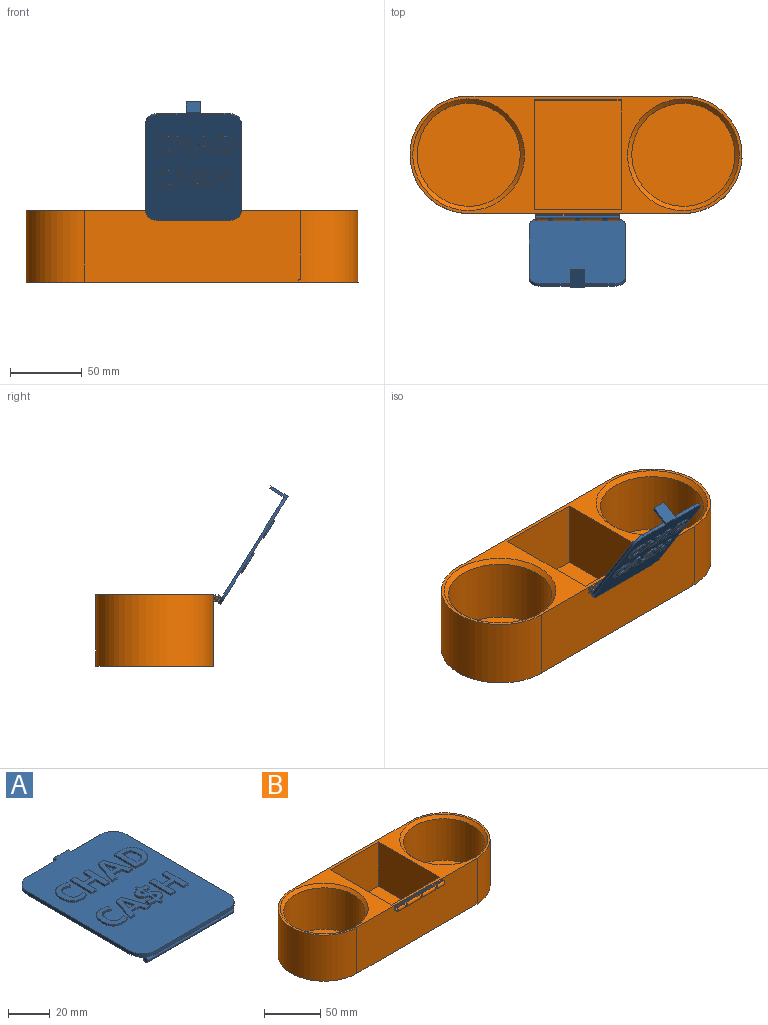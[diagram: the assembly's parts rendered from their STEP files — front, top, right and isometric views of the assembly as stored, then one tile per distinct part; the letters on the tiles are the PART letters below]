
ASSEMBLY  parts=2 mates=1
PART A: 167 faces, bbox 67.2x89x15 mm
  f0: plane 88.97x67.19mm, normal (0,0,1), area 4974.1mm2, adj f1,f6,f7,f8,f9,f22,f23,f24
  f1: plane 20.08x2mm, normal (0,1,0), area 40.2mm2, adj f0,f5,f23,f28
  f2: cylinder r=1.4mm len=58.64mm, axis (-1,0,0), area 502.5mm2, adj f3,f4,f10,f11,f12,f13,f14,f15
  f3: plane 2.8x2.8mm, normal (1,0,0), area 6.2mm2, adj f2
  f4: plane 2.8x2.8mm, normal (-1,0,0), area 6.2mm2, adj f2
  f5: plane 86.97x67.19mm, normal (0,0,-1), area 5768mm2, adj f1,f6,f7,f8,f9,f10,f11,f12
  f6: plane 50.01x2mm, normal (0,-1,0), area 100mm2, adj f0,f5,f22,f24
  f7: plane 20.08x2mm, normal (0,1,0), area 40.2mm2, adj f0,f5,f25,f29
  f8: plane 69.79x2mm, normal (1,0,0), area 139.6mm2, adj f0,f5,f24,f25
  f9: plane 69.79x2mm, normal (-1,0,0), area 139.6mm2, adj f0,f5,f22,f23
  f10: plane 2x1.6mm, normal (1,0,0), area 2.6mm2, adj f2,f5,f11,f13
  f11: plane 2x1.6mm, normal (0,-1,0), area 3.2mm2, adj f2,f5,f10,f12
  f12: plane 2x1.6mm, normal (-1,0,0), area 2.6mm2, adj f2,f5,f11,f13
  f13: plane 2x1.59mm, normal (0,1,0), area 3.2mm2, adj f2,f5,f10,f12
  f14: plane 2x1.59mm, normal (0,1,0), area 3.2mm2, adj f2,f5,f15,f17
  f15: plane 2x1.6mm, normal (1,0,0), area 2.6mm2, adj f2,f5,f14,f16
  f16: plane 2x1.6mm, normal (0,-1,0), area 3.2mm2, adj f2,f5,f15,f17
  f17: plane 2x1.6mm, normal (-1,0,0), area 2.6mm2, adj f2,f5,f14,f16
  f18: plane 2x1.59mm, normal (0,1,0), area 3.2mm2, adj f2,f5,f19,f21
  f19: plane 2x1.6mm, normal (1,0,0), area 2.6mm2, adj f2,f5,f18,f20
  f20: plane 2x1.6mm, normal (0,-1,0), area 3.2mm2, adj f2,f5,f19,f21
  f21: plane 2x1.6mm, normal (-1,0,0), area 2.6mm2, adj f2,f5,f18,f20
  f22: cylinder r=8.59mm len=8.59mm, axis (0,0,1), area 27mm2, adj f0,f5,f6,f9
  f23: cylinder r=8.59mm len=8.59mm, axis (0,0,-1), area 27mm2, adj f0,f1,f5,f9
  f24: cylinder r=8.59mm len=8.59mm, axis (0,0,-1), area 27mm2, adj f0,f5,f6,f8
  f25: cylinder r=8.59mm len=8.59mm, axis (0,0,1), area 27mm2, adj f0,f5,f7,f8
  f26: plane 12.02x9.85mm, normal (0,-1,0), area 118.4mm2, adj f5,f27,f28,f29
  f27: plane 9.85x2mm, normal (0,0,-1), area 19.7mm2, adj f26,f28,f29,f30
  f28: plane 14.02x2mm, normal (-1,0,0), area 28mm2, adj f0,f1,f26,f27,f30
  f29: plane 14.02x2mm, normal (1,0,0), area 28mm2, adj f0,f7,f26,f27,f30
  f30: plane 14.02x9.85mm, normal (0,1,0), area 138.1mm2, adj f0,f27,f28,f29
  f31: extruded ~2.7x1.31mm, area 3.1mm2, adj f0,f32,f45,f46
  f32: extruded ~1.62x1mm, area 1.7mm2, adj f0,f31,f33,f46
  f33: extruded ~1.65x1mm, area 1.8mm2, adj f0,f32,f34,f46
  f34: plane 2.51x1mm, normal (0.93,-0.37,0), area 2.7mm2, adj f0,f33,f35,f46
  f35: extruded ~4.27x1.02mm, area 4.4mm2, adj f0,f34,f36,f46
  f36: extruded ~3.63x1mm, area 3.8mm2, adj f0,f35,f37,f46
  f37: extruded ~2.62x2.38mm, area 3.6mm2, adj f0,f36,f38,f46
  f38: extruded ~3.99x1mm, area 4.1mm2, adj f0,f37,f39,f46
  f39: extruded ~5.54x1.68mm, area 5.9mm2, adj f0,f38,f40,f46
  f40: extruded ~4.87x1.93mm, area 5.4mm2, adj f0,f39,f41,f46
  f41: extruded ~4.01x1mm, area 4.1mm2, adj f0,f40,f42,f46
  f42: plane 2.59x1mm, normal (1,0,0), area 2.6mm2, adj f0,f41,f43,f46
  f43: extruded ~3.72x1mm, area 3.8mm2, adj f0,f42,f44,f46
  f44: extruded ~4.88x3.66mm, area 7mm2, adj f0,f43,f45,f46
  f45: extruded ~3.65x1mm, area 3.8mm2, adj f0,f31,f44,f46
  f46: plane 14.99x11.11mm, normal (0,0,1), area 74.6mm2, adj f31,f32,f33,f34,f35,f36,f37,f38
  f47: plane 3.08x1mm, normal (0,-1,0), area 3.1mm2, adj f0,f48,f58,f59
  f48: plane 14.58x1mm, normal (1,0,0), area 14.6mm2, adj f0,f47,f49,f59
  f49: plane 3.08x1mm, normal (0,1,0), area 3.1mm2, adj f0,f48,f50,f59
  f50: plane 5.71x1mm, normal (-1,0,0), area 5.7mm2, adj f0,f49,f51,f59
  f51: plane 5.77x1mm, normal (0,1,0), area 5.8mm2, adj f0,f50,f52,f59
  f52: plane 5.71x1mm, normal (1,0,0), area 5.7mm2, adj f0,f51,f53,f59
  f53: plane 3.09x1mm, normal (0,1,0), area 3.1mm2, adj f0,f52,f54,f59
  f54: plane 14.58x1mm, normal (-1,0,0), area 14.6mm2, adj f0,f53,f55,f59
  f55: plane 3.09x1mm, normal (0,-1,0), area 3.1mm2, adj f0,f54,f56,f59
  f56: plane 6.29x1mm, normal (1,0,0), area 6.3mm2, adj f0,f55,f57,f59
  f57: plane 5.77x1mm, normal (0,-1,0), area 5.8mm2, adj f0,f56,f58,f59
  f58: plane 6.29x1mm, normal (-1,0,0), area 6.3mm2, adj f0,f47,f57,f59
  f59: plane 14.58x11.95mm, normal (0,0,1), area 104.8mm2, adj f47,f48,f49,f50,f51,f52,f53,f54
  f60: extruded ~5.33x1.65mm, area 5.6mm2, adj f61,f71,f72,f73
  f61: plane 3.8x1mm, normal (0,1,0), area 3.8mm2, adj f60,f62,f72,f73
  f62: extruded ~6.31x1.88mm, area 6.6mm2, adj f61,f71,f72,f73
  f63: plane 3.47x1.06mm, normal (-0.96,-0.29,0), area 3.6mm2, adj f0,f64,f70,f72
  f64: plane 3.33x1mm, normal (0,-1,0), area 3.3mm2, adj f0,f63,f65,f72
  f65: plane 14.64x5.17mm, normal (0.94,0.33,0), area 15.5mm2, adj f0,f64,f66,f72
  f66: plane 3.78x1mm, normal (0,1,0), area 3.8mm2, adj f0,f65,f67,f72
  f67: plane 14.64x5.15mm, normal (-0.94,0.33,0), area 15.5mm2, adj f0,f66,f68,f72
  f68: plane 3.33x1mm, normal (0,-1,0), area 3.3mm2, adj f0,f67,f69,f72
  f69: plane 3.47x1.06mm, normal (0.96,-0.29,0), area 3.6mm2, adj f0,f68,f70,f72
  f70: plane 5.32x1mm, normal (0,-1,0), area 5.3mm2, adj f0,f63,f69,f72
  f71: extruded ~1x0.98mm, area 1mm2, adj f60,f62,f72,f73
  f72: plane 14.64x14.09mm, normal (0,0,1), area 96.9mm2, adj f60,f61,f62,f63,f64,f65,f66,f67
  f73: plane 6.31x3.8mm, normal (0,0,1), area 11.8mm2, adj f60,f61,f62,f71
  f74: extruded ~4.7x4.15mm, area 7.2mm2, adj f75,f85,f86,f87
  f75: extruded ~4.8x4.47mm, area 7.5mm2, adj f74,f76,f86,f87
  f76: plane 1.32x1mm, normal (0,1,0), area 1.3mm2, adj f75,f77,f86,f87
  f77: plane 9.49x1mm, normal (1,0,0), area 9.5mm2, adj f76,f85,f86,f87
  f78: extruded ~5.51x2.05mm, area 6.1mm2, adj f0,f79,f84,f86
  f79: extruded ~5.27x1.98mm, area 5.8mm2, adj f0,f78,f80,f86
  f80: extruded ~5.55x1.88mm, area 6mm2, adj f0,f79,f81,f86
  f81: plane 4.58x1mm, normal (0,1,0), area 4.6mm2, adj f0,f80,f82,f86
  f82: plane 14.58x1mm, normal (-1,0,0), area 14.6mm2, adj f0,f81,f83,f86
  f83: plane 4.13x1mm, normal (0,-1,0), area 4.1mm2, adj f0,f82,f84,f86
  f84: extruded ~5.92x1.91mm, area 6.4mm2, adj f0,f78,f83,f86
  f85: plane 1.64x1mm, normal (0,-1,0), area 1.6mm2, adj f74,f77,f86,f87
  f86: plane 14.58x12.1mm, normal (0,0,1), area 108.2mm2, adj f74,f75,f76,f77,f78,f79,f80,f81
  f87: plane 9.49x5.79mm, normal (0,0,1), area 48.1mm2, adj f74,f75,f76,f77,f85
  f88: extruded ~2.7x1.31mm, area 3.1mm2, adj f0,f89,f102,f103
  f89: extruded ~1.62x1mm, area 1.7mm2, adj f0,f88,f90,f103
  f90: extruded ~1.65x1mm, area 1.8mm2, adj f0,f89,f91,f103
  f91: plane 2.51x1mm, normal (0.93,-0.37,0), area 2.7mm2, adj f0,f90,f92,f103
  f92: extruded ~4.27x1.02mm, area 4.4mm2, adj f0,f91,f93,f103
  f93: extruded ~3.63x1mm, area 3.8mm2, adj f0,f92,f94,f103
  f94: extruded ~2.62x2.38mm, area 3.6mm2, adj f0,f93,f95,f103
  f95: extruded ~3.99x1mm, area 4.1mm2, adj f0,f94,f96,f103
  f96: extruded ~5.54x1.68mm, area 5.9mm2, adj f0,f95,f97,f103
  f97: extruded ~4.87x1.93mm, area 5.4mm2, adj f0,f96,f98,f103
  f98: extruded ~4.01x1mm, area 4.1mm2, adj f0,f97,f99,f103
  f99: plane 2.59x1mm, normal (1,0,0), area 2.6mm2, adj f0,f98,f100,f103
  f100: extruded ~3.72x1mm, area 3.8mm2, adj f0,f99,f101,f103
  f101: extruded ~4.88x3.66mm, area 7mm2, adj f0,f100,f102,f103
  f102: extruded ~3.65x1mm, area 3.8mm2, adj f0,f88,f101,f103
  f103: plane 14.99x11.11mm, normal (0,0,1), area 74.6mm2, adj f88,f89,f90,f91,f92,f93,f94,f95
  f104: extruded ~5.33x1.65mm, area 5.6mm2, adj f105,f115,f116,f117
  f105: plane 3.8x1mm, normal (0,1,0), area 3.8mm2, adj f104,f106,f116,f117
  f106: extruded ~6.31x1.88mm, area 6.6mm2, adj f105,f115,f116,f117
  f107: plane 3.47x1.06mm, normal (-0.96,-0.29,0), area 3.6mm2, adj f0,f108,f114,f116
  f108: plane 3.33x1mm, normal (0,-1,0), area 3.3mm2, adj f0,f107,f109,f116
  f109: plane 14.64x5.17mm, normal (0.94,0.33,0), area 15.5mm2, adj f0,f108,f110,f116
  f110: plane 3.78x1mm, normal (0,1,0), area 3.8mm2, adj f0,f109,f111,f116
  f111: plane 14.64x5.15mm, normal (-0.94,0.33,0), area 15.5mm2, adj f0,f110,f112,f116
  f112: plane 3.33x1mm, normal (0,-1,0), area 3.3mm2, adj f0,f111,f113,f116
  f113: plane 3.47x1.06mm, normal (0.96,-0.29,0), area 3.6mm2, adj f0,f112,f114,f116
  f114: plane 5.32x1mm, normal (0,-1,0), area 5.3mm2, adj f0,f107,f113,f116
  f115: extruded ~1x0.98mm, area 1mm2, adj f104,f106,f116,f117
  f116: plane 14.64x14.09mm, normal (0,0,1), area 96.9mm2, adj f104,f105,f106,f107,f108,f109,f110,f111
  f117: plane 6.31x3.8mm, normal (0,0,1), area 11.8mm2, adj f104,f105,f106,f115
  f118: extruded ~1x0.72mm, area 0.8mm2, adj f119,f150,f151,f152
  f119: extruded ~1.29x1.04mm, area 1.8mm2, adj f118,f120,f151,f152
  f120: plane 2.34x1mm, normal (-1,0,0), area 2.3mm2, adj f119,f150,f151,f152
  f121: extruded ~1x0.71mm, area 0.8mm2, adj f122,f148,f151,f153
  f122: extruded ~1.36x1.17mm, area 2mm2, adj f121,f123,f151,f153
  f123: plane 2.48x1mm, normal (1,0,0), area 2.5mm2, adj f122,f148,f151,f153
  f124: extruded ~2.55x1.15mm, area 2.9mm2, adj f0,f125,f149,f151
  f125: extruded ~1.54x1mm, area 1.6mm2, adj f0,f124,f126,f151
  f126: extruded ~1.21x1.21mm, area 1.7mm2, adj f0,f125,f127,f151
  f127: extruded ~2.77x1.3mm, area 3.1mm2, adj f0,f126,f128,f151
  f128: plane 2.94x1mm, normal (1,0,0), area 2.9mm2, adj f0,f127,f129,f151
  f129: extruded ~3.19x1mm, area 3.3mm2, adj f0,f128,f130,f151
  f130: plane 2.33x1mm, normal (0.93,-0.37,0), area 2.5mm2, adj f0,f129,f131,f151
  f131: extruded ~4.13x1mm, area 4.3mm2, adj f0,f130,f132,f151
  f132: plane 1.48x1mm, normal (1,0,0), area 1.5mm2, adj f0,f131,f133,f151
  f133: plane 1.37x1mm, normal (0,1,0), area 1.4mm2, adj f0,f132,f134,f151
  f134: plane 1.53x1mm, normal (-1,0,0), area 1.5mm2, adj f0,f133,f135,f151
  f135: extruded ~3.16x1.13mm, area 3.4mm2, adj f0,f134,f136,f151
  f136: extruded ~2.38x1.13mm, area 2.7mm2, adj f0,f135,f137,f151
  f137: extruded ~2.26x1mm, area 2.5mm2, adj f0,f136,f138,f151
  f138: extruded ~2.8x1.69mm, area 3.3mm2, adj f0,f137,f139,f151
  f139: plane 1x0.67mm, normal (-0.36,-0.93,0), area 0.7mm2, adj f0,f138,f140,f151
  f140: plane 3.09x1mm, normal (-1,0,0), area 3.1mm2, adj f0,f139,f141,f151
  f141: extruded ~2.18x1mm, area 2.2mm2, adj f0,f140,f142,f151
  f142: extruded ~2.09x1mm, area 2.2mm2, adj f0,f141,f143,f151
  f143: plane 2.63x1mm, normal (-1,0,0), area 2.6mm2, adj f0,f142,f144,f151
  f144: extruded ~4.27x1mm, area 4.4mm2, adj f0,f143,f145,f151
  f145: plane 2x1mm, normal (-1,0,0), area 2mm2, adj f0,f144,f146,f151
  f146: plane 1.37x1mm, normal (0,-1,0), area 1.4mm2, adj f0,f145,f147,f151
  f147: plane 2.05x1mm, normal (1,0,0), area 2mm2, adj f0,f146,f149,f151
  f148: extruded ~1.02x1mm, area 1.2mm2, adj f121,f123,f151,f153
  f149: extruded ~3.21x1.15mm, area 3.5mm2, adj f0,f124,f147,f151
  f150: extruded ~1x0.98mm, area 1.1mm2, adj f118,f120,f151,f152
  f151: plane 16.68x10.01mm, normal (0,0,1), area 88.4mm2, adj f118,f119,f120,f121,f122,f123,f124,f125
  f152: plane 2.34x1.29mm, normal (0,0,1), area 2.2mm2, adj f118,f119,f120,f150
  f153: plane 2.48x1.36mm, normal (0,0,1), area 2.4mm2, adj f121,f122,f123,f148
  f154: plane 3.08x1mm, normal (0,-1,0), area 3.1mm2, adj f0,f155,f165,f166
  f155: plane 14.58x1mm, normal (1,0,0), area 14.6mm2, adj f0,f154,f156,f166
  f156: plane 3.08x1mm, normal (0,1,0), area 3.1mm2, adj f0,f155,f157,f166
  f157: plane 5.71x1mm, normal (-1,0,0), area 5.7mm2, adj f0,f156,f158,f166
  f158: plane 5.77x1mm, normal (0,1,0), area 5.8mm2, adj f0,f157,f159,f166
  f159: plane 5.71x1mm, normal (1,0,0), area 5.7mm2, adj f0,f158,f160,f166
  f160: plane 3.09x1mm, normal (0,1,0), area 3.1mm2, adj f0,f159,f161,f166
  f161: plane 14.58x1mm, normal (-1,0,0), area 14.6mm2, adj f0,f160,f162,f166
  f162: plane 3.09x1mm, normal (0,-1,0), area 3.1mm2, adj f0,f161,f163,f166
  f163: plane 6.29x1mm, normal (1,0,0), area 6.3mm2, adj f0,f162,f164,f166
  f164: plane 5.77x1mm, normal (0,-1,0), area 5.8mm2, adj f0,f163,f165,f166
  f165: plane 6.29x1mm, normal (-1,0,0), area 6.3mm2, adj f0,f154,f164,f166
  f166: plane 14.58x11.95mm, normal (0,0,1), area 104.8mm2, adj f154,f155,f156,f157,f158,f159,f160,f161
PART B: 41 faces, bbox 232x87x50 mm
  f0: plane 58.64x2.5mm, normal (0,0,-1), area 144.7mm2, adj f5,f6,f7,f8,f9,f24,f26,f30
  f1: cylinder r=1.5mm len=58.64mm, axis (-1,0,0), area 381.1mm2, adj f2,f3,f4,f8,f24,f25,f29,f30
  f2: plane 16x1.2mm, normal (0,1,0), area 19.2mm2, adj f1,f5,f32,f38
  f3: plane 8.82x1.2mm, normal (0,1,0), area 10.6mm2, adj f1,f6,f8,f35
  f4: plane 16x1.2mm, normal (0,1,0), area 19.2mm2, adj f1,f7,f31,f34
  f5: cylinder r=2.5mm len=16mm, axis (-1,0,0), area 108.2mm2, adj f0,f2,f32,f38
  f6: cylinder r=2.5mm len=8.82mm, axis (-1,0,0), area 59.6mm2, adj f0,f3,f8,f35
  f7: cylinder r=2.5mm len=16mm, axis (-1,0,0), area 108.2mm2, adj f0,f4,f31,f34
  f8: plane 5x4.77mm, normal (1,0,0), area 12.1mm2, adj f0,f1,f3,f6,f9,f27,f28,f29
  f9: plane 150.76x50.01mm, normal (0,-1,0), area 7270.4mm2, adj f0,f8,f16,f18,f21,f23,f24,f27
  f10: plane 72x72mm, normal (0,0,1), area 4071.5mm2, adj f20
  f11: plane 72x72mm, normal (0,0,1), area 4071.5mm2, adj f19
  f12: plane 60.56x48mm, normal (0,1,0), area 2906.9mm2, adj f13,f15,f21,f22
  f13: plane 76.6x48mm, normal (-1,0,0), area 3677mm2, adj f12,f14,f21,f22
  f14: plane 60.56x48mm, normal (0,-1,0), area 2906.9mm2, adj f13,f15,f21,f22
  f15: plane 76.6x48mm, normal (1,0,0), area 3677mm2, adj f12,f14,f21,f22
  f16: cylinder r=41mm len=82mm, axis (0,0,-1), area 6406.9mm2, adj f9,f17,f21,f23
  f17: plane 147.66x50mm, normal (0,1,0), area 7383.1mm2, adj f16,f18,f21,f23
  f18: cylinder r=41mm len=82mm, axis (0,0,-1), area 6556.4mm2, adj f9,f17,f21,f23
  f19: cylinder r=36mm len=72mm, axis (0,0,-1), area 10178.8mm2, adj f11,f39
  f20: cylinder r=36mm len=72mm, axis (0,0,-1), area 10178.8mm2, adj f10,f40
  f21: plane 232x82mm, normal (0,0,1), area 3379.7mm2, adj f9,f12,f13,f14,f15,f16,f17,f18
  f22: plane 76.6x60.56mm, normal (0,0,1), area 4639.2mm2, adj f12,f13,f14,f15
  f23: plane 232.01x82.01mm, normal (0,0,-1), area 17575.6mm2, adj f9,f16,f17,f18
  f24: plane 5x4.77mm, normal (-1,0,0), area 12.1mm2, adj f0,f1,f9,f25,f26,f27,f28,f29
  f25: plane 8.82x1.2mm, normal (0,1,0), area 10.6mm2, adj f1,f24,f26,f37
  f26: cylinder r=2.5mm len=8.82mm, axis (-1,0,0), area 59.7mm2, adj f0,f24,f25,f37
  f27: cylinder r=0.86mm len=58.64mm, axis (-1,0,0), area 49mm2, adj f8,f9,f24,f28
  f28: cylinder r=2.5mm len=58.64mm, axis (-1,0,0), area 47mm2, adj f8,f24,f27,f29
  f29: plane 58.64x1.2mm, normal (0,-1,0), area 70.5mm2, adj f1,f8,f24,f28
  f30: plane 3x1.02mm, normal (0,-1,0), area 3mm2, adj f0,f1,f31,f32
  f31: plane 4.77x2.71mm, normal (-1,0,0), area 5.4mm2, adj f0,f1,f4,f7,f30
  f32: plane 4.77x2.71mm, normal (1,0,0), area 5.4mm2, adj f0,f1,f2,f5,f30
  f33: plane 3x1.01mm, normal (0,-1,0), area 3mm2, adj f0,f1,f34,f35
  f34: plane 4.77x2.71mm, normal (1,0,0), area 5.4mm2, adj f0,f1,f4,f7,f33
  f35: plane 4.77x2.71mm, normal (-1,0,0), area 5.4mm2, adj f0,f1,f3,f6,f33
  f36: plane 3x1.02mm, normal (0,-1,0), area 3mm2, adj f0,f1,f37,f38
  f37: plane 4.77x2.71mm, normal (1,0,0), area 5.4mm2, adj f0,f1,f25,f26,f36
  f38: plane 4.77x2.71mm, normal (-1,0,0), area 5.4mm2, adj f0,f1,f2,f5,f36
  f39: cone r=36mm half-angle=45deg, axis (0,0,1), area 999.6mm2, adj f19,f21
  f40: cone r=36mm half-angle=45deg, axis (0,0,1), area 999.6mm2, adj f20,f21
PLACE A rot(axis=(1,0,0),121.9deg) t=(0.01,162.8,3.65)mm
PLACE B rot(axis=(0,-0.56,-0.83),0deg) t=(0.01,160.19,-89.9)mm
MATE revolute A.f2 <-> B.f1  axis (1,0,0) through (38.47,135.52,-42.4)mm
